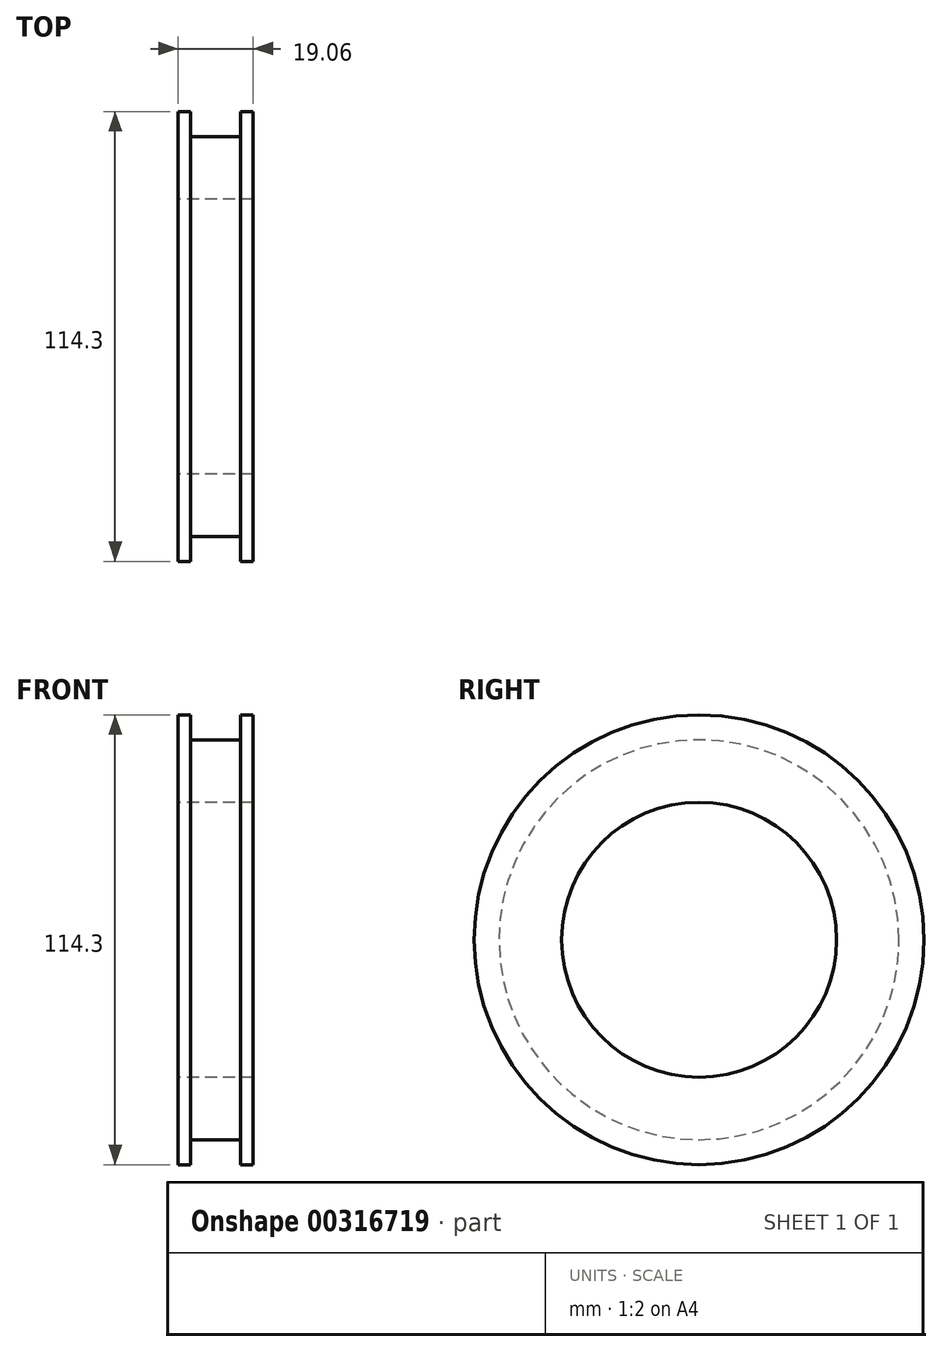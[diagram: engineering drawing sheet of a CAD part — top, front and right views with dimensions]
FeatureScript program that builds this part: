
annotation { "Feature Type Name" : "Feature", "Feature Type Description" : "" }
export const myFeature = defineFeature(function(context is Context, id is Id, definition is map)
    precondition{}
    {
        {
            var Q0;
            Q0=qCreatedBy(makeId("Right.planeOp"),FACE);
            var sketch = newSketch(context, id + "F0", { "sketchPlane" : qUnion([Q0])});
            skCircle(sketch, "E0", {"center": v(0, 0) * mm, "radius": 50.8 * mm});
            skCircle(sketch, "E1", {"center": v(0, 0) * mm, "radius": 34.93 * mm});
            skSolve(sketch);
        }
        {
            var Q0;
            Q0 = qSketchRegion(id + "F0", true);
            extrude(context, id + "F1", {"entities" : qUnion([Q0]), "endBound" : BoundingType.SYMMETRIC, "depth" : 12.7 * mm});
        }
        {
            var Q0;
            Q0=makeQuery(id+"F1.opExtrude","CAP_FACE",FACE,{"disambiguationData":[OSD([sQuery(id+"F0.wireOp",EDGE,"E0"),sQuery(id+"F0.wireOp",EDGE,"E1")])],"isStart":false});
            var sketch = newSketch(context, id + "F2", { "sketchPlane" : qUnion([Q0])});
            skCircle(sketch, "E2.0", {"center": v(0, 0) * mm, "radius": 34.93 * mm});
            skCircle(sketch, "E3", {"center": v(0, 0) * mm, "radius": 57.15 * mm});
            skSolve(sketch);
        }
        {
            var Q0;
            Q0 = qSketchRegion(id + "F2", true);
            extrude(context, id + "F3", {"entities" : qUnion([Q0]), "depth" : 3.17 * mm});
        }
        {
            var Q0;
            Q0=makeQuery(id+"F3.opExtrude","SWEPT_BODY",BODY,{"disambiguationData":[OSD([sQuery(id+"F2.wireOp",EDGE,"E2.0"),sQuery(id+"F2.wireOp",EDGE,"E3")])]});
            var Q1;
            Q1=qCreatedBy(makeId("Right.planeOp"),FACE);
            mirror(context, id + "F4", {"operationType" : NewBodyOperationType.ADD, "entities" : qUnion([Q0]), "mirrorPlane" : qUnion([Q1])});
        }
    });
